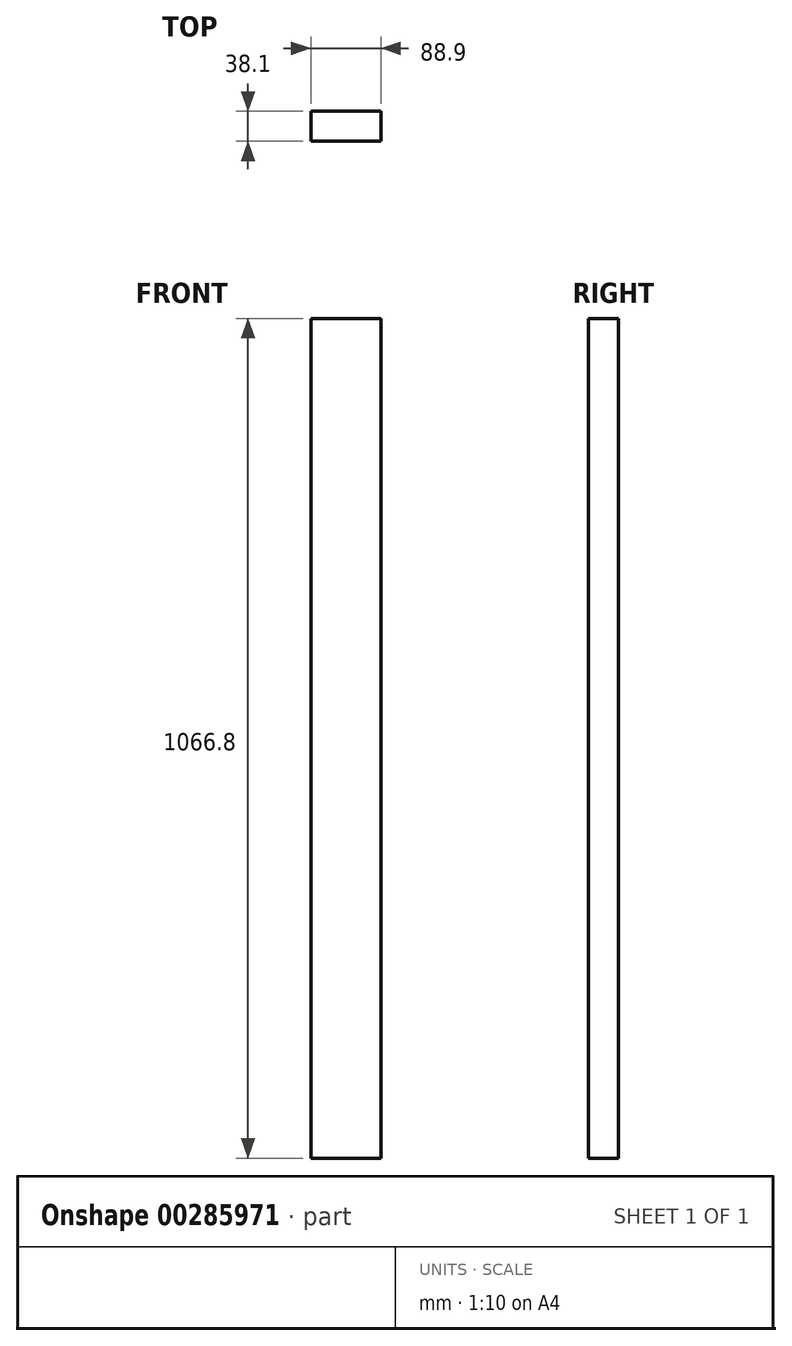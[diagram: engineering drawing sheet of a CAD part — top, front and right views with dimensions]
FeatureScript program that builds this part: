
annotation { "Feature Type Name" : "Feature", "Feature Type Description" : "" }
export const myFeature = defineFeature(function(context is Context, id is Id, definition is map)
    precondition{}
    {
        {
            var Q0;
            Q0=qCreatedBy(makeId("Top.planeOp"),FACE);
            var sketch = newSketch(context, id + "F0", { "sketchPlane" : qUnion([Q0])});
            skLineSegment(sketch, "E0.bottom", {"start": v(44.45, -19.05) * mm, "end": v(-44.45, -19.05) * mm});
            skLineSegment(sketch, "E0.top", {"start": v(44.45, 19.05) * mm, "end": v(-44.45, 19.05) * mm});
            skLineSegment(sketch, "E0.left", {"start": v(44.45, -19.05) * mm, "end": v(44.45, 19.05) * mm});
            skLineSegment(sketch, "E0.right", {"start": v(-44.45, -19.05) * mm, "end": v(-44.45, 19.05) * mm});
            skPoint(sketch, "E0.middle", {"position": v(0, 0) * mm});
            skSolve(sketch);
        }
        {
            var Q0;
            Q0=makeQuery(id+"F0.imprint","IMPRINT",FACE,{"disambiguationData":[TD([[makeQuery(id+"F0.imprint","IMPRINT",EDGE,{"derivedFrom":sQuery(id+"F0.wireOp",EDGE,"E0.bottom")}),-1.0]])]});
            extrude(context, id + "F1", {"entities" : qUnion([Q0]), "depth" : 1066.8 * mm});
        }
    });
